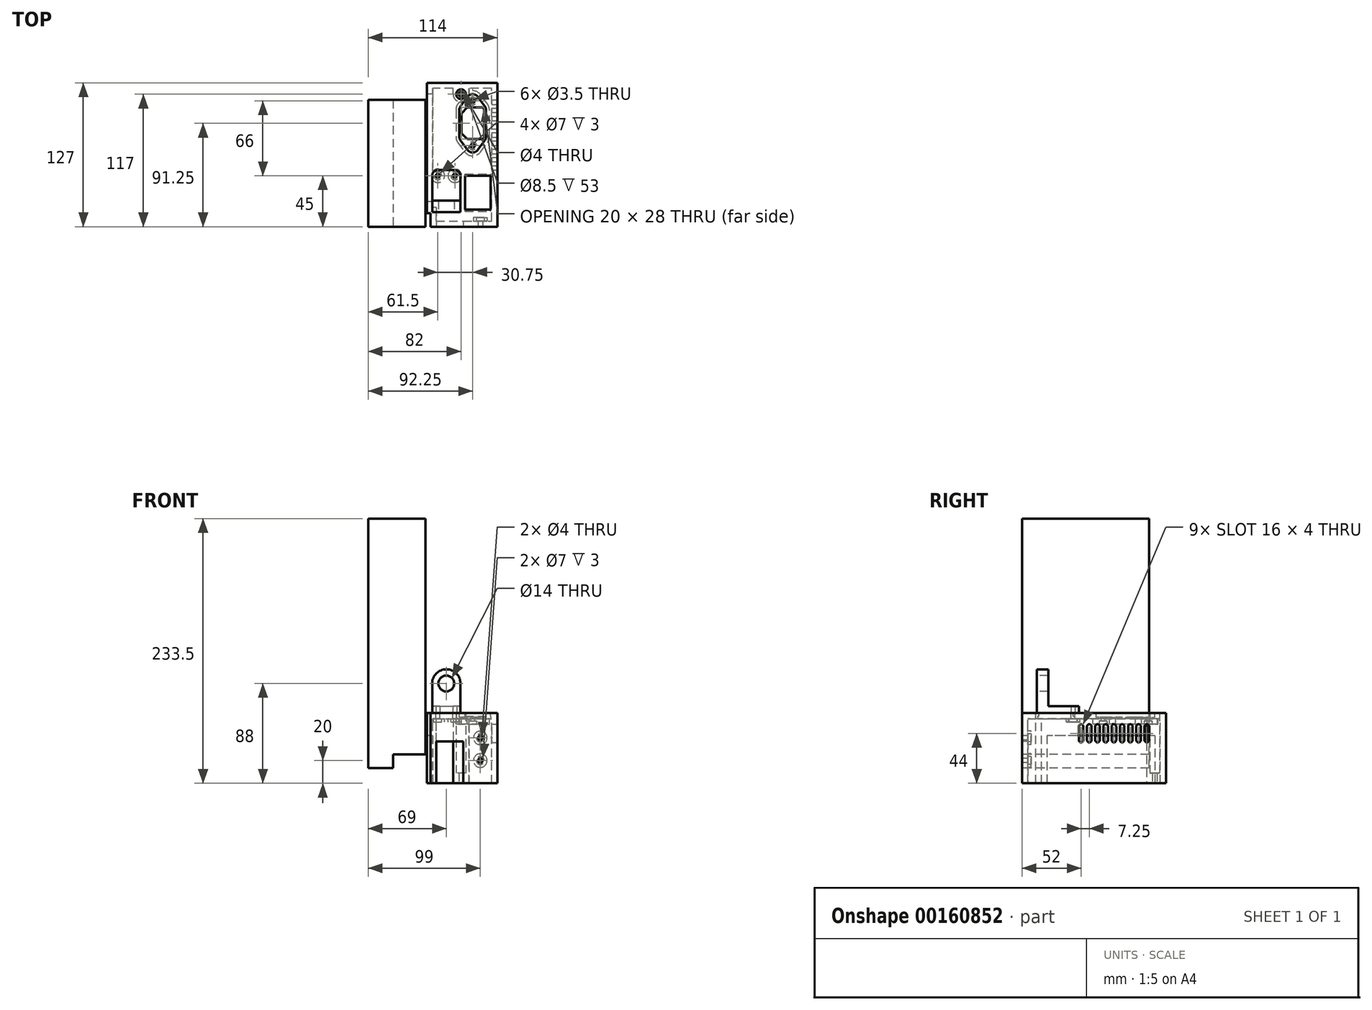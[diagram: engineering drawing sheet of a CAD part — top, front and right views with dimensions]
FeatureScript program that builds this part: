
annotation { "Feature Type Name" : "Feature", "Feature Type Description" : "" }
export const myFeature = defineFeature(function(context is Context, id is Id, definition is map)
    precondition{}
    {
        {
            var Q0;
            Q0=qCreatedBy(makeId("Front.planeOp"),FACE);
            var sketch = newSketch(context, id + "F0", { "sketchPlane" : qUnion([Q0])});
            skLineSegment(sketch, "E0", {"start": v(0, 13.5) * mm, "end": v(0, 233.5) * mm});
            skLineSegment(sketch, "E1", {"start": v(0, 233.5) * mm, "end": v(50.5, 233.5) * mm});
            skLineSegment(sketch, "E2", {"start": v(50.5, 233.5) * mm, "end": v(50.5, 25.5) * mm});
            skLineSegment(sketch, "E3", {"start": v(50.5, 25.5) * mm, "end": v(22, 25.5) * mm});
            skLineSegment(sketch, "E4", {"start": v(22, 25.5) * mm, "end": v(22, 13.5) * mm});
            skLineSegment(sketch, "E5", {"start": v(22, 13.5) * mm, "end": v(0, 13.5) * mm});
            skSolve(sketch);
        }
        {
            var Q0;
            Q0=qCreatedBy(makeId("Top.planeOp"),FACE);
            cPlane(context, id + "F1", {"entities" : qUnion([Q0]), "cplaneType" : CPlaneType.OFFSET, "offset" : 62 * mm, "width" : 150 * mm, "height" : 150 * mm});
        }
        {
            assignVariable(context, id + "F2", {"name" : "X", "anyValue" : 5});
        }
        {
            var Q0;
            Q0=qCreatedBy(id+"F1.planeOp",FACE);
            var sketch = newSketch(context, id + "F3", { "sketchPlane" : qUnion([Q0])});
            skLineSegment(sketch, "E6", {"start": v(55, 0) * mm, "end": v(114, 0) * mm});
            skLineSegment(sketch, "E7", {"start": v(114, 0) * mm, "end": v(114, 127) * mm});
            skLineSegment(sketch, "E8", {"start": v(114, 127) * mm, "end": v(52, 127) * mm});
            skLineSegment(sketch, "E9", {"start": v(52, 127) * mm, "end": v(52, 12) * mm});
            skLineSegment(sketch, "E10.bottom", {"start": v(85.5, 15) * mm, "end": v(108, 15) * mm});
            skLineSegment(sketch, "E10.top", {"start": v(85.5, 45) * mm, "end": v(108, 45) * mm});
            skLineSegment(sketch, "E10.left", {"start": v(85.5, 15) * mm, "end": v(85.5, 45) * mm});
            skLineSegment(sketch, "E10.right", {"start": v(108, 15) * mm, "end": v(108, 45) * mm});
            skLineSegment(sketch, "E11", {"start": v(52, 12) * mm, "end": v(55, 12) * mm});
            skLineSegment(sketch, "E12", {"start": v(55, 12) * mm, "end": v(55, 0) * mm});
            skPoint(sketch, "E13.orphan", {"position": v(52, 0) * mm});
            skCircle(sketch, "E14", {"center": v(61.5, 45) * mm, "radius": 1.75 * mm});
            skCircle(sketch, "E15", {"center": v(76.5, 45) * mm, "radius": 1.75 * mm});
            skLineSegment(sketch, "E16", {"start": v(61.5, 45) * mm, "end": v(76.5, 45) * mm, "construction": true});
            skPoint(sketch, "E17", {"position": v(69, 45) * mm});
            skPoint(sketch, "E18", {"position": v(83, 127) * mm});
            skSolve(sketch);
        }
        {
            var Q0;
            Q0 = qSketchRegion(id + "F3", true);
            extrude(context, id + "F4", {"entities" : qUnion([Q0]), "oppositeDirection" : true, "depth" : (getVariable(context, 'X')) * mm});
        }
        {
            var Q0;
            Q0=makeQuery(id+"F4.opExtrude","CAP_FACE",FACE,{"disambiguationData":[OSD([sQuery(id+"F3.wireOp",EDGE,"E6"),sQuery(id+"F3.wireOp",EDGE,"E7"),sQuery(id+"F3.wireOp",EDGE,"E8"),sQuery(id+"F3.wireOp",EDGE,"E9"),sQuery(id+"F3.wireOp",EDGE,"E10.bottom"),sQuery(id+"F3.wireOp",EDGE,"E10.top"),sQuery(id+"F3.wireOp",EDGE,"E10.left"),sQuery(id+"F3.wireOp",EDGE,"E10.right"),sQuery(id+"F3.wireOp",EDGE,"E11"),sQuery(id+"F3.wireOp",EDGE,"E12"),sQuery(id+"F3.wireOp",EDGE,"E14"),sQuery(id+"F3.wireOp",EDGE,"E15")])],"isStart":false});
            var sketch = newSketch(context, id + "F5", { "sketchPlane" : qUnion([Q0]), "disableImprinting" : false});
            skLineSegment(sketch, "E19", {"start": v(85.5, -30) * mm, "end": v(108, -30) * mm, "construction": true});
            skLineSegment(sketch, "E20.bottom", {"start": v(85.5, -45) * mm, "end": v(108, -45) * mm});
            skLineSegment(sketch, "E20.top", {"start": v(85.5, -46.5) * mm, "end": v(108, -46.5) * mm});
            skLineSegment(sketch, "E20.left", {"start": v(85.5, -45) * mm, "end": v(85.5, -46.5) * mm});
            skLineSegment(sketch, "E20.right", {"start": v(108, -45) * mm, "end": v(108, -46.5) * mm});
            skLineSegment(sketch, "E21.MirrorCS", {"start": v(108, -15) * mm, "end": v(108, -13.5) * mm});
            skLineSegment(sketch, "E22.MirrorCS", {"start": v(85.5, -15) * mm, "end": v(85.5, -13.5) * mm});
            skLineSegment(sketch, "E23.MirrorCS", {"start": v(85.5, -15) * mm, "end": v(108, -15) * mm});
            skLineSegment(sketch, "E24.MirrorCS", {"start": v(85.5, -13.5) * mm, "end": v(108, -13.5) * mm});
            skSolve(sketch);
        }
        {
            var Q0;
            Q0 = qSketchRegion(id + "F5", true);
            extrude(context, id + "F6", {"entities" : qUnion([Q0]), "operationType" : NewBodyOperationType.REMOVE, "oppositeDirection" : true, "depth" : 2 * mm});
        }
        {
            var Q0;
            Q0=makeQuery(id+"F4.opExtrude","SWEPT_FACE",FACE,{"disambiguationData":[OSD([sQuery(id+"F3.wireOp",EDGE,"E6")])]});
            var sketch = newSketch(context, id + "F7", { "sketchPlane" : qUnion([Q0])});
            skLineSegment(sketch, "E25.bottom", {"start": v(55, 57) * mm, "end": v(114, 57) * mm});
            skLineSegment(sketch, "E25.left", {"start": v(55, 57) * mm, "end": v(55, 37) * mm});
            skLineSegment(sketch, "E25.right", {"start": v(114, 57) * mm, "end": v(114, 0) * mm});
            skLineSegment(sketch, "E26", {"start": v(55, 37) * mm, "end": v(84, 37) * mm});
            skLineSegment(sketch, "E27", {"start": v(84, 37) * mm, "end": v(84, 0) * mm});
            skLineSegment(sketch, "E28", {"start": v(84, 0) * mm, "end": v(114, 0) * mm});
            skCircle(sketch, "E29", {"center": v(99, 20) * mm, "radius": 2 * mm});
            skCircle(sketch, "E30", {"center": v(99, 40) * mm, "radius": 2 * mm});
            skPoint(sketch, "E31", {"position": v(99, 0) * mm});
            skSolve(sketch);
        }
        {
            var Q0;
            Q0 = qSketchRegion(id + "F7", true);
            extrude(context, id + "F8", {"entities" : qUnion([Q0]), "operationType" : NewBodyOperationType.ADD, "oppositeDirection" : true, "depth" : (getVariable(context, 'X')) * mm});
        }
        {
            var Q0;
            Q0=makeQuery(id+"F4.opExtrude","CAP_FACE",FACE,{"disambiguationData":[OSD([sQuery(id+"F3.wireOp",EDGE,"E6"),sQuery(id+"F3.wireOp",EDGE,"E7"),sQuery(id+"F3.wireOp",EDGE,"E8"),sQuery(id+"F3.wireOp",EDGE,"E9"),sQuery(id+"F3.wireOp",EDGE,"E10.bottom"),sQuery(id+"F3.wireOp",EDGE,"E10.top"),sQuery(id+"F3.wireOp",EDGE,"E10.left"),sQuery(id+"F3.wireOp",EDGE,"E10.right"),sQuery(id+"F3.wireOp",EDGE,"E11"),sQuery(id+"F3.wireOp",EDGE,"E12")])],"isStart":false});
            var sketch = newSketch(context, id + "F9", { "sketchPlane" : qUnion([Q0])});
            skLineSegment(sketch, "E32", {"start": v(114, -5) * mm, "end": v(114, -127) * mm});
            skLineSegment(sketch, "E33", {"start": v(114, -127) * mm, "end": v(52, -127) * mm});
            skLineSegment(sketch, "E34", {"start": v(52, -127) * mm, "end": v(52, -12) * mm});
            skLineSegment(sketch, "E35", {"start": v(52, -12) * mm, "end": v(55, -12) * mm});
            skLineSegment(sketch, "E36", {"start": v(55, -12) * mm, "end": v(55, 0) * mm});
            skLineSegment(sketch, "E37", {"start": v(55, 0) * mm, "end": v(60, 0) * mm});
            skLineSegment(sketch, "E38", {"start": v(60, 0) * mm, "end": v(60, -17) * mm});
            skLineSegment(sketch, "E39", {"start": v(60, -17) * mm, "end": v(57, -17) * mm});
            skLineSegment(sketch, "E40", {"start": v(57, -122) * mm, "end": v(109, -122) * mm});
            skLineSegment(sketch, "E41", {"start": v(109, -122) * mm, "end": v(109, -5) * mm});
            skLineSegment(sketch, "E42", {"start": v(109, -5) * mm, "end": v(114, -5) * mm});
            skLineSegment(sketch, "E43", {"start": v(57, -17) * mm, "end": v(57, -122) * mm});
            skSolve(sketch);
        }
        {
            var Q0;
            Q0 = qSketchRegion(id + "F9", true);
            var Q1;
            Q1=qCreatedBy(makeId("Top.planeOp"),FACE);
            extrude(context, id + "F10", {"entities" : qUnion([Q0]), "operationType" : NewBodyOperationType.ADD, "endBound" : BoundingType.UP_TO_SURFACE, "endBoundEntityFace" : qUnion([Q1]), "depth" : 25 * mm});
        }
        {
            var Q0;
            Q0=qCreatedBy(makeId("Top.planeOp"),FACE);
            var sketch = newSketch(context, id + "F11", { "sketchPlane" : qUnion([Q0])});
            skCircle(sketch, "E44", {"center": v(82, 117) * mm, "radius": 7 * mm});
            skPoint(sketch, "E45", {"position": v(52, 127) * mm});
            skCircle(sketch, "E46", {"center": v(82, 117) * mm, "radius": 2 * mm});
            skLineSegment(sketch, "E47", {"start": v(75, 117) * mm, "end": v(75, 127) * mm});
            skLineSegment(sketch, "E48", {"start": v(75, 127) * mm, "end": v(89, 127) * mm});
            skLineSegment(sketch, "E49", {"start": v(89, 127) * mm, "end": v(89, 117) * mm});
            skSolve(sketch);
        }
        {
            var Q0;
            Q0 = qSketchRegion(id + "F11", true);
            var Q1;
            Q1=makeQuery(id+"F4.opExtrude","CAP_FACE",FACE,{"disambiguationData":[OSD([sQuery(id+"F3.wireOp",EDGE,"E6"),sQuery(id+"F3.wireOp",EDGE,"E7"),sQuery(id+"F3.wireOp",EDGE,"E8"),sQuery(id+"F3.wireOp",EDGE,"E9"),sQuery(id+"F3.wireOp",EDGE,"E10.bottom"),sQuery(id+"F3.wireOp",EDGE,"E10.top"),sQuery(id+"F3.wireOp",EDGE,"E10.left"),sQuery(id+"F3.wireOp",EDGE,"E10.right"),sQuery(id+"F3.wireOp",EDGE,"E11"),sQuery(id+"F3.wireOp",EDGE,"E12"),sQuery(id+"F3.wireOp",EDGE,"E14"),sQuery(id+"F3.wireOp",EDGE,"E15")])],"isStart":true});
            extrude(context, id + "F12", {"entities" : qUnion([Q0]), "operationType" : NewBodyOperationType.ADD, "endBound" : BoundingType.UP_TO_SURFACE, "endBoundEntityFace" : qUnion([Q1]), "depth" : 25 * mm});
        }
        {
            var Q0;
            Q0=makeQuery(id+"F4.opExtrude","CAP_FACE",FACE,{"disambiguationData":[OSD([sQuery(id+"F3.wireOp",EDGE,"E6"),sQuery(id+"F3.wireOp",EDGE,"E7"),sQuery(id+"F3.wireOp",EDGE,"E8"),sQuery(id+"F3.wireOp",EDGE,"E9"),sQuery(id+"F3.wireOp",EDGE,"E10.bottom"),sQuery(id+"F3.wireOp",EDGE,"E10.top"),sQuery(id+"F3.wireOp",EDGE,"E10.left"),sQuery(id+"F3.wireOp",EDGE,"E10.right"),sQuery(id+"F3.wireOp",EDGE,"icFeodHG-X67S-GUbe-anhc-zYEM1fz8yry0"),sQuery(id+"F3.wireOp",EDGE,"6k1QtSXw-TwQi-QSg0-uvi8-0hQTAuIMNpvk"),sQuery(id+"F3.wireOp",EDGE,"tgVIdKk2-un53-9VJQ-DeHb-1WSuqyKC1VRE"),sQuery(id+"F3.wireOp",EDGE,"f23b5b03-630f-4854-9769-42faad0535ed0.MirrorCS"),sQuery(id+"F3.wireOp",EDGE,"a012bc5f-21a9-49e4-83e2-b8ed56f6d75a0.MirrorCS"),sQuery(id+"F3.wireOp",EDGE,"6c684b62-b8df-48bf-a682-26947638c5150.MirrorCS"),sQuery(id+"F3.wireOp",EDGE,"226860c7-e29d-4859-8903-939a02a947c00.MirrorCS"),sQuery(id+"F3.wireOp",EDGE,"a3930372-3e52-4283-94ea-4f7785915df50.MirrorCS"),sQuery(id+"F3.wireOp",EDGE,"2bd0807f-86d2-4633-a58d-4318a14e78250.MirrorCS"),sQuery(id+"F3.wireOp",EDGE,"e933c2e2-a1c3-460c-bcf3-0e9317d1bf4b0.MirrorCS"),sQuery(id+"F3.wireOp",EDGE,"0f086fad-6bdd-4517-966f-ae18f11ac6380.MirrorCS"),sQuery(id+"F3.wireOp",EDGE,"3b35046c-a394-40a0-8ea3-9ca372d3b10c0.MirrorCS"),sQuery(id+"F3.wireOp",EDGE,"92acfec4-3e32-4bdd-830b-4b1668f26de1.filletArc"),sQuery(id+"F3.wireOp",EDGE,"2ca518d5-96dd-47ef-80e1-5cfa871b5b48.filletArc"),sQuery(id+"F3.wireOp",EDGE,"7e7fc31b-50f3-40aa-b3ab-8119e1af2ef3.filletArc"),sQuery(id+"F3.wireOp",EDGE,"9d7bcf72-4d73-4a1d-98b1-cddff58b6144.filletArc")])],"isStart":true});
            var sketch = newSketch(context, id + "F13", { "sketchPlane" : qUnion([Q0])});
            skLineSegment(sketch, "E50", {"start": v(92.25, 117) * mm, "end": v(92.25, 91.25) * mm, "construction": true});
            skLineSegment(sketch, "E51", {"start": v(92.25, 91.25) * mm, "end": v(104, 91.25) * mm, "construction": true});
            skLineSegment(sketch, "E52", {"start": v(104, 91.25) * mm, "end": v(104, 103.01) * mm});
            skLineSegment(sketch, "E53", {"start": v(102.81, 106.6) * mm, "end": v(96.75, 114.74) * mm});
            skArc(sketch, "E54", {"start": v(96.75, 114.74) * mm, "mid": v(94.77, 116.4) * mm, "end": v(92.25, 117) * mm});
            skArc(sketch, "E55.MirrorCS", {"start": v(87.75, 114.74) * mm, "mid": v(89.73, 116.4) * mm, "end": v(92.25, 117) * mm});
            skLineSegment(sketch, "E56.MirrorCS", {"start": v(81.69, 106.6) * mm, "end": v(87.75, 114.74) * mm});
            skLineSegment(sketch, "E57.MirrorCS", {"start": v(80.5, 91.25) * mm, "end": v(80.5, 103.01) * mm});
            skLineSegment(sketch, "E58.MirrorCS", {"start": v(80.5, 91.25) * mm, "end": v(80.5, 79.49) * mm});
            skLineSegment(sketch, "E59.MirrorCS", {"start": v(81.69, 75.9) * mm, "end": v(87.75, 67.76) * mm});
            skArc(sketch, "E60.MirrorCS", {"start": v(87.75, 67.76) * mm, "mid": v(89.73, 66.1) * mm, "end": v(92.25, 65.5) * mm});
            skArc(sketch, "E61.MirrorCS", {"start": v(96.75, 67.76) * mm, "mid": v(94.77, 66.1) * mm, "end": v(92.25, 65.5) * mm});
            skLineSegment(sketch, "E62.MirrorCS", {"start": v(102.81, 75.9) * mm, "end": v(96.75, 67.76) * mm});
            skLineSegment(sketch, "E63.MirrorCS", {"start": v(104, 91.25) * mm, "end": v(104, 79.49) * mm});
            skCircle(sketch, "E64", {"center": v(92.25, 111) * mm, "radius": 1.75 * mm, "construction": true});
            skCircle(sketch, "E65.MirrorC", {"center": v(92.25, 71.5) * mm, "radius": 1.75 * mm, "construction": true});
            skPoint(sketch, "E66.visualSharp", {"position": v(104, 105) * mm});
            skArc(sketch, "E66.filletArc", {"start": v(104, 103.01) * mm, "mid": v(103.7, 104.9) * mm, "end": v(102.81, 106.6) * mm});
            skPoint(sketch, "E67.visualSharp", {"position": v(80.5, 105) * mm});
            skArc(sketch, "E67.filletArc", {"start": v(81.69, 106.6) * mm, "mid": v(80.8, 104.9) * mm, "end": v(80.5, 103.01) * mm});
            skPoint(sketch, "E68.visualSharp", {"position": v(80.5, 77.5) * mm});
            skArc(sketch, "E68.filletArc", {"start": v(80.5, 79.49) * mm, "mid": v(80.8, 77.6) * mm, "end": v(81.69, 75.9) * mm});
            skPoint(sketch, "E69.visualSharp", {"position": v(104, 77.5) * mm});
            skArc(sketch, "E69.filletArc", {"start": v(102.81, 75.9) * mm, "mid": v(103.7, 77.6) * mm, "end": v(104, 79.49) * mm});
            skSolve(sketch);
        }
        {
            var Q0;
            Q0 = qSketchRegion(id + "F13", true);
            extrude(context, id + "F14", {"entities" : qUnion([Q0]), "operationType" : NewBodyOperationType.REMOVE, "oppositeDirection" : true, "depth" : 3.8 * mm});
        }
        {
            var Q0;
            Q0=makeQuery(id+"F14.boolean.opBoolean","COPY",FACE,{"derivedFrom":makeQuery(id+"F14.opExtrude","CAP_FACE",FACE,{"disambiguationData":[OSD([sQuery(id+"F13.wireOp",EDGE,"E52"),sQuery(id+"F13.wireOp",EDGE,"E53"),sQuery(id+"F13.wireOp",EDGE,"E54"),sQuery(id+"F13.wireOp",EDGE,"E55.MirrorCS"),sQuery(id+"F13.wireOp",EDGE,"E56.MirrorCS"),sQuery(id+"F13.wireOp",EDGE,"E57.MirrorCS"),sQuery(id+"F13.wireOp",EDGE,"E58.MirrorCS"),sQuery(id+"F13.wireOp",EDGE,"E59.MirrorCS"),sQuery(id+"F13.wireOp",EDGE,"E60.MirrorCS"),sQuery(id+"F13.wireOp",EDGE,"E61.MirrorCS"),sQuery(id+"F13.wireOp",EDGE,"E62.MirrorCS"),sQuery(id+"F13.wireOp",EDGE,"E63.MirrorCS"),sQuery(id+"F13.wireOp",EDGE,"E66.filletArc"),sQuery(id+"F13.wireOp",EDGE,"E67.filletArc"),sQuery(id+"F13.wireOp",EDGE,"E68.filletArc"),sQuery(id+"F13.wireOp",EDGE,"E69.filletArc")])],"isStart":false})});
            var sketch = newSketch(context, id + "F15", { "sketchPlane" : qUnion([Q0])});
            skPoint(sketch, "E70", {"position": v(92.25, 91.25) * mm});
            skLineSegment(sketch, "E71", {"start": v(102.25, 91.25) * mm, "end": v(102.25, 103.25) * mm});
            skLineSegment(sketch, "E72", {"start": v(100.25, 105.25) * mm, "end": v(87.5, 105.25) * mm});
            skLineSegment(sketch, "E73", {"start": v(87.5, 105.25) * mm, "end": v(82.25, 100) * mm});
            skLineSegment(sketch, "E74", {"start": v(82.25, 100) * mm, "end": v(82.25, 91.25) * mm});
            skLineSegment(sketch, "E75", {"start": v(82.25, 91.25) * mm, "end": v(102.25, 91.25) * mm, "construction": true});
            skLineSegment(sketch, "E76.MirrorCS", {"start": v(82.25, 82.5) * mm, "end": v(82.25, 91.25) * mm});
            skLineSegment(sketch, "E77.MirrorCS", {"start": v(87.5, 77.25) * mm, "end": v(82.25, 82.5) * mm});
            skLineSegment(sketch, "E78.MirrorCS", {"start": v(100.25, 77.25) * mm, "end": v(87.5, 77.25) * mm});
            skLineSegment(sketch, "E79.MirrorCS", {"start": v(102.25, 91.25) * mm, "end": v(102.25, 79.25) * mm});
            skCircle(sketch, "E80", {"center": v(92.25, 111) * mm, "radius": 1.75 * mm});
            skCircle(sketch, "E81.MirrorC", {"center": v(92.25, 71.5) * mm, "radius": 1.75 * mm});
            skPoint(sketch, "E82.visualSharp", {"position": v(102.25, 105.25) * mm});
            skArc(sketch, "E82.filletArc", {"start": v(102.25, 103.25) * mm, "mid": v(101.66, 104.66) * mm, "end": v(100.25, 105.25) * mm});
            skPoint(sketch, "E83.visualSharp", {"position": v(102.25, 77.25) * mm});
            skArc(sketch, "E83.filletArc", {"start": v(100.25, 77.25) * mm, "mid": v(101.66, 77.84) * mm, "end": v(102.25, 79.25) * mm});
            skSolve(sketch);
        }
        {
            var Q0;
            Q0 = qSketchRegion(id + "F15", true);
            extrude(context, id + "F16", {"entities" : qUnion([Q0]), "operationType" : NewBodyOperationType.REMOVE, "oppositeDirection" : true, "depth" : 25 * mm});
        }
        {
            var Q0;
            Q0=makeQuery(id+"F4.opExtrude","CAP_FACE",FACE,{"disambiguationData":[OSD([sQuery(id+"F3.wireOp",EDGE,"E6"),sQuery(id+"F3.wireOp",EDGE,"E7"),sQuery(id+"F3.wireOp",EDGE,"E8"),sQuery(id+"F3.wireOp",EDGE,"E9"),sQuery(id+"F3.wireOp",EDGE,"E10.bottom"),sQuery(id+"F3.wireOp",EDGE,"E10.top"),sQuery(id+"F3.wireOp",EDGE,"E10.left"),sQuery(id+"F3.wireOp",EDGE,"E10.right")])],"isStart":false});
            var sketch = newSketch(context, id + "F17", { "sketchPlane" : qUnion([Q0])});
            skArc(sketch, "E84.0", {"start": v(105.22, -74.11) * mm, "mid": v(106.54, -76.66) * mm, "end": v(107, -79.49) * mm});
            skLineSegment(sketch, "E84.1", {"start": v(99.16, -65.97) * mm, "end": v(105.22, -74.11) * mm});
            skArc(sketch, "E84.2", {"start": v(92.25, -62.5) * mm, "mid": v(96.11, -63.42) * mm, "end": v(99.16, -65.97) * mm});
            skArc(sketch, "E84.3", {"start": v(85.34, -65.97) * mm, "mid": v(88.39, -63.42) * mm, "end": v(92.25, -62.5) * mm});
            skLineSegment(sketch, "E84.4", {"start": v(79.28, -74.11) * mm, "end": v(85.34, -65.97) * mm});
            skArc(sketch, "E84.5", {"start": v(99.16, -116.53) * mm, "mid": v(96.11, -119.08) * mm, "end": v(92.25, -120) * mm});
            skLineSegment(sketch, "E84.6", {"start": v(105.22, -108.39) * mm, "end": v(99.16, -116.53) * mm});
            skArc(sketch, "E84.7", {"start": v(107, -103.01) * mm, "mid": v(106.54, -105.84) * mm, "end": v(105.22, -108.39) * mm});
            skLineSegment(sketch, "E84.8", {"start": v(107, -89.5) * mm, "end": v(107, -103.01) * mm});
            skArc(sketch, "E84.9", {"start": v(92.25, -120) * mm, "mid": v(88.39, -119.08) * mm, "end": v(85.34, -116.53) * mm});
            skLineSegment(sketch, "E84.10", {"start": v(85.34, -116.53) * mm, "end": v(79.28, -108.39) * mm});
            skArc(sketch, "E84.11", {"start": v(79.28, -108.39) * mm, "mid": v(77.96, -105.84) * mm, "end": v(77.5, -103.01) * mm});
            skLineSegment(sketch, "E84.12", {"start": v(77.5, -103.01) * mm, "end": v(77.5, -89.5) * mm});
            skLineSegment(sketch, "E84.13", {"start": v(77.5, -89.5) * mm, "end": v(77.5, -79.49) * mm});
            skLineSegment(sketch, "E84.14", {"start": v(107, -79.49) * mm, "end": v(107, -89.5) * mm});
            skArc(sketch, "E84.15", {"start": v(77.5, -79.49) * mm, "mid": v(77.96, -76.66) * mm, "end": v(79.28, -74.11) * mm});
            skLineSegment(sketch, "E85", {"start": v(100.25, -105.25) * mm, "end": v(87.5, -105.25) * mm});
            skLineSegment(sketch, "E86", {"start": v(87.5, -105.25) * mm, "end": v(82.25, -100) * mm});
            skLineSegment(sketch, "E87", {"start": v(82.25, -100) * mm, "end": v(82.25, -82.5) * mm});
            skLineSegment(sketch, "E88", {"start": v(82.25, -82.5) * mm, "end": v(87.5, -77.25) * mm});
            skLineSegment(sketch, "E89", {"start": v(87.5, -77.25) * mm, "end": v(100.25, -77.25) * mm});
            skArc(sketch, "E90", {"start": v(102.25, -79.25) * mm, "mid": v(101.66, -77.84) * mm, "end": v(100.25, -77.25) * mm});
            skArc(sketch, "E91", {"start": v(100.25, -105.25) * mm, "mid": v(101.66, -104.66) * mm, "end": v(102.25, -103.25) * mm});
            skLineSegment(sketch, "E92", {"start": v(102.25, -103.25) * mm, "end": v(102.25, -79.25) * mm});
            skCircle(sketch, "E93", {"center": v(92.25, -111) * mm, "radius": 1.75 * mm});
            skCircle(sketch, "E94", {"center": v(92.25, -71.5) * mm, "radius": 1.75 * mm});
            skSolve(sketch);
        }
        {
            var Q0;
            Q0 = qSketchRegion(id + "F17", true);
            extrude(context, id + "F18", {"entities" : qUnion([Q0]), "operationType" : NewBodyOperationType.ADD, "depth" : 5 * mm});
        }
        {
            var Q0;
            Q0=qCreatedBy(makeId("Top.planeOp"),FACE);
            var sketch = newSketch(context, id + "F19", { "sketchPlane" : qUnion([Q0])});
            skCircle(sketch, "E95", {"center": v(82, 117) * mm, "radius": 4.25 * mm});
            skSolve(sketch);
        }
        {
            var Q0;
            Q0 = qSketchRegion(id + "F19", true);
            extrude(context, id + "F20", {"entities" : qUnion([Q0]), "operationType" : NewBodyOperationType.REMOVE, "endBound" : BoundingType.THROUGH_ALL, "depth" : 25 * mm, "hasSecondDirection" : true, "secondDirectionOppositeDirection" : false, "secondDirectionDepth" : 9 * mm});
        }
        {
            var Q0;
            Q0 = qSketchRegion(id + "F0", true);
            extrude(context, id + "F21", {"entities" : qUnion([Q0]), "oppositeDirection" : true, "depth" : 112 * mm});
        }
        {
            var Q0;
            Q0=makeQuery(id+"F10.boolean.opBoolean","MERGE",FACE,{"derivedFrom":[makeQuery(id+"F4.opExtrude","SWEPT_FACE",FACE,{"disambiguationData":[OSD([sQuery(id+"F3.wireOp",EDGE,"E9")])]}),makeQuery(id+"F10.opExtrude","SWEPT_FACE",FACE,{"disambiguationData":[OSD([sQuery(id+"F9.wireOp",EDGE,"E34")])]})]});
            var sketch = newSketch(context, id + "F22", { "sketchPlane" : qUnion([Q0])});
            skLineSegment(sketch, "E96.bottom", {"start": v(-117, 42) * mm, "end": v(-22, 42) * mm});
            skLineSegment(sketch, "E96.top", {"start": v(-117, 0) * mm, "end": v(-22, 0) * mm});
            skLineSegment(sketch, "E96.left", {"start": v(-117, 42) * mm, "end": v(-117, 0) * mm});
            skLineSegment(sketch, "E96.right", {"start": v(-22, 42) * mm, "end": v(-22, 0) * mm});
            skSolve(sketch);
        }
        {
            var Q0;
            Q0 = qSketchRegion(id + "F22", true);
            var Q1;
            Q1=makeQuery(id+"F10.opExtrude","SWEPT_FACE",FACE,{"disambiguationData":[OSD([sQuery(id+"F9.wireOp",EDGE,"E43")])]});
            extrude(context, id + "F23", {"entities" : qUnion([Q0]), "operationType" : NewBodyOperationType.REMOVE, "flatOperationType" : FlatOperationType.REMOVE, "endBound" : BoundingType.UP_TO_SURFACE, "oppositeDirection" : true, "endBoundEntityFace" : qUnion([Q1]), "offsetDistance" : 25 * mm, "depth" : 25 * mm, "domain" : OperationDomain.MODEL});
        }
        {
            var Q0;
            Q0=makeQuery(id+"F18.opExtrude","CAP_FACE",FACE,{"disambiguationData":[OSD([sQuery(id+"F17.wireOp",EDGE,"E84.0"),sQuery(id+"F17.wireOp",EDGE,"E84.1"),sQuery(id+"F17.wireOp",EDGE,"E84.2"),sQuery(id+"F17.wireOp",EDGE,"E84.3"),sQuery(id+"F17.wireOp",EDGE,"E84.4"),sQuery(id+"F17.wireOp",EDGE,"E84.5"),sQuery(id+"F17.wireOp",EDGE,"E84.6"),sQuery(id+"F17.wireOp",EDGE,"E84.7"),sQuery(id+"F17.wireOp",EDGE,"E84.8"),sQuery(id+"F17.wireOp",EDGE,"E84.9"),sQuery(id+"F17.wireOp",EDGE,"E84.10"),sQuery(id+"F17.wireOp",EDGE,"E84.11"),sQuery(id+"F17.wireOp",EDGE,"E84.12"),sQuery(id+"F17.wireOp",EDGE,"E84.13"),sQuery(id+"F17.wireOp",EDGE,"E84.14"),sQuery(id+"F17.wireOp",EDGE,"E84.15"),sQuery(id+"F17.wireOp",EDGE,"E85"),sQuery(id+"F17.wireOp",EDGE,"E86"),sQuery(id+"F17.wireOp",EDGE,"E87"),sQuery(id+"F17.wireOp",EDGE,"E88"),sQuery(id+"F17.wireOp",EDGE,"E89"),sQuery(id+"F17.wireOp",EDGE,"E90"),sQuery(id+"F17.wireOp",EDGE,"E91"),sQuery(id+"F17.wireOp",EDGE,"E92"),sQuery(id+"F17.wireOp",EDGE,"E93"),sQuery(id+"F17.wireOp",EDGE,"E94")])],"isStart":false});
            var sketch = newSketch(context, id + "F24", { "sketchPlane" : qUnion([Q0])});
            skCircle(sketch, "E97", {"center": v(92.25, -71.5) * mm, "radius": 3.5 * mm});
            skCircle(sketch, "E98", {"center": v(92.25, -111) * mm, "radius": 3.5 * mm});
            skSolve(sketch);
        }
        {
            var Q0;
            Q0 = qSketchRegion(id + "F24", true);
            extrude(context, id + "F25", {"entities" : qUnion([Q0]), "operationType" : NewBodyOperationType.REMOVE, "oppositeDirection" : true, "depth" : 3 * mm});
        }
        {
            var Q0;
            Q0=makeQuery(id+"F4.opExtrude","CAP_FACE",FACE,{"disambiguationData":[OSD([sQuery(id+"F3.wireOp",EDGE,"E6"),sQuery(id+"F3.wireOp",EDGE,"E7"),sQuery(id+"F3.wireOp",EDGE,"E8"),sQuery(id+"F3.wireOp",EDGE,"E9"),sQuery(id+"F3.wireOp",EDGE,"E10.bottom"),sQuery(id+"F3.wireOp",EDGE,"E10.top"),sQuery(id+"F3.wireOp",EDGE,"E10.left"),sQuery(id+"F3.wireOp",EDGE,"E10.right"),sQuery(id+"F3.wireOp",EDGE,"E11"),sQuery(id+"F3.wireOp",EDGE,"E12"),sQuery(id+"F3.wireOp",EDGE,"E14"),sQuery(id+"F3.wireOp",EDGE,"E15")])],"isStart":false});
            var sketch = newSketch(context, id + "F26", { "sketchPlane" : qUnion([Q0])});
            skCircle(sketch, "E99", {"center": v(76.5, -45) * mm, "radius": 3.5 * mm});
            skCircle(sketch, "E100", {"center": v(76.5, -45) * mm, "radius": 6 * mm});
            skLineSegment(sketch, "E101", {"start": v(76.5, -45) * mm, "end": v(61.5, -45) * mm, "construction": true});
            skLineSegment(sketch, "E102", {"start": v(69, -45) * mm, "end": v(69, -39.5) * mm, "construction": true});
            skCircle(sketch, "E103.MirrorC", {"center": v(61.5, -45) * mm, "radius": 6 * mm});
            skCircle(sketch, "E104.MirrorC", {"center": v(61.5, -45) * mm, "radius": 3.5 * mm});
            skSolve(sketch);
        }
        {
            var Q0;
            Q0 = qSketchRegion(id + "F26", true);
            extrude(context, id + "F27", {"entities" : qUnion([Q0]), "operationType" : NewBodyOperationType.ADD, "depth" : 3 * mm});
        }
        {
            var Q0;
            Q0=makeQuery(id+"F10.boolean.opBoolean","MERGE",FACE,{"derivedFrom":[makeQuery(id+"F8.boolean.opBoolean","MERGE",FACE,{"derivedFrom":[makeQuery(id+"F4.opExtrude","SWEPT_FACE",FACE,{"disambiguationData":[OSD([sQuery(id+"F3.wireOp",EDGE,"E7")])]}),makeQuery(id+"F8.opExtrude","SWEPT_FACE",FACE,{"disambiguationData":[OSD([sQuery(id+"F7.wireOp",EDGE,"E25.right")])]})]}),makeQuery(id+"F10.opExtrude","SWEPT_FACE",FACE,{"disambiguationData":[OSD([sQuery(id+"F9.wireOp",EDGE,"E32")])]})]});
            var sketch = newSketch(context, id + "F28", { "sketchPlane" : qUnion([Q0])});
            skLineSegment(sketch, "E105", {"start": v(50, 50) * mm, "end": v(50, 38) * mm});
            skLineSegment(sketch, "E106", {"start": v(54, 50) * mm, "end": v(54, 38) * mm});
            skArc(sketch, "E107", {"start": v(54, 50) * mm, "mid": v(52, 52) * mm, "end": v(50, 50) * mm});
            skArc(sketch, "E108", {"start": v(50, 38) * mm, "mid": v(52, 36) * mm, "end": v(54, 38) * mm});
            skPoint(sketch, "E109", {"position": v(52, 52) * mm});
            skArc(sketch, "E110.1.0.0", {"start": v(57.25, 38) * mm, "mid": v(59.25, 36) * mm, "end": v(61.25, 38) * mm});
            skLineSegment(sketch, "E110.1.0.1", {"start": v(61.25, 50) * mm, "end": v(61.25, 38) * mm});
            skLineSegment(sketch, "E110.1.0.2", {"start": v(57.25, 50) * mm, "end": v(57.25, 38) * mm});
            skPoint(sketch, "E110.1.0.3", {"position": v(59.25, 52) * mm});
            skArc(sketch, "E110.1.0.4", {"start": v(61.25, 50) * mm, "mid": v(59.25, 52) * mm, "end": v(57.25, 50) * mm});
            skArc(sketch, "E110.2.0.0", {"start": v(64.5, 38) * mm, "mid": v(66.5, 36) * mm, "end": v(68.5, 38) * mm});
            skLineSegment(sketch, "E110.2.0.1", {"start": v(68.5, 50) * mm, "end": v(68.5, 38) * mm});
            skLineSegment(sketch, "E110.2.0.2", {"start": v(64.5, 50) * mm, "end": v(64.5, 38) * mm});
            skPoint(sketch, "E110.2.0.3", {"position": v(66.5, 52) * mm});
            skArc(sketch, "E110.2.0.4", {"start": v(68.5, 50) * mm, "mid": v(66.5, 52) * mm, "end": v(64.5, 50) * mm});
            skArc(sketch, "E110.3.0.0", {"start": v(71.75, 38) * mm, "mid": v(73.75, 36) * mm, "end": v(75.75, 38) * mm});
            skLineSegment(sketch, "E110.3.0.1", {"start": v(75.75, 50) * mm, "end": v(75.75, 38) * mm});
            skLineSegment(sketch, "E110.3.0.2", {"start": v(71.75, 50) * mm, "end": v(71.75, 38) * mm});
            skPoint(sketch, "E110.3.0.3", {"position": v(73.75, 52) * mm});
            skArc(sketch, "E110.3.0.4", {"start": v(75.75, 50) * mm, "mid": v(73.75, 52) * mm, "end": v(71.75, 50) * mm});
            skArc(sketch, "E110.4.0.0", {"start": v(79, 38) * mm, "mid": v(81, 36) * mm, "end": v(83, 38) * mm});
            skLineSegment(sketch, "E110.4.0.1", {"start": v(83, 50) * mm, "end": v(83, 38) * mm});
            skLineSegment(sketch, "E110.4.0.2", {"start": v(79, 50) * mm, "end": v(79, 38) * mm});
            skPoint(sketch, "E110.4.0.3", {"position": v(81, 52) * mm});
            skArc(sketch, "E110.4.0.4", {"start": v(83, 50) * mm, "mid": v(81, 52) * mm, "end": v(79, 50) * mm});
            skArc(sketch, "E110.5.0.0", {"start": v(86.25, 38) * mm, "mid": v(88.25, 36) * mm, "end": v(90.25, 38) * mm});
            skLineSegment(sketch, "E110.5.0.1", {"start": v(90.25, 50) * mm, "end": v(90.25, 38) * mm});
            skLineSegment(sketch, "E110.5.0.2", {"start": v(86.25, 50) * mm, "end": v(86.25, 38) * mm});
            skPoint(sketch, "E110.5.0.3", {"position": v(88.25, 52) * mm});
            skArc(sketch, "E110.5.0.4", {"start": v(90.25, 50) * mm, "mid": v(88.25, 52) * mm, "end": v(86.25, 50) * mm});
            skArc(sketch, "E110.6.0.0", {"start": v(93.5, 38) * mm, "mid": v(95.5, 36) * mm, "end": v(97.5, 38) * mm});
            skLineSegment(sketch, "E110.6.0.1", {"start": v(97.5, 50) * mm, "end": v(97.5, 38) * mm});
            skLineSegment(sketch, "E110.6.0.2", {"start": v(93.5, 50) * mm, "end": v(93.5, 38) * mm});
            skPoint(sketch, "E110.6.0.3", {"position": v(95.5, 52) * mm});
            skArc(sketch, "E110.6.0.4", {"start": v(97.5, 50) * mm, "mid": v(95.5, 52) * mm, "end": v(93.5, 50) * mm});
            skArc(sketch, "E110.7.0.0", {"start": v(100.75, 38) * mm, "mid": v(102.75, 36) * mm, "end": v(104.75, 38) * mm});
            skLineSegment(sketch, "E110.7.0.1", {"start": v(104.75, 50) * mm, "end": v(104.75, 38) * mm});
            skLineSegment(sketch, "E110.7.0.2", {"start": v(100.75, 50) * mm, "end": v(100.75, 38) * mm});
            skPoint(sketch, "E110.7.0.3", {"position": v(102.75, 52) * mm});
            skArc(sketch, "E110.7.0.4", {"start": v(104.75, 50) * mm, "mid": v(102.75, 52) * mm, "end": v(100.75, 50) * mm});
            skLineSegment(sketch, "E110.direction1", {"start": v(50, 38) * mm, "end": v(57.25, 38) * mm, "construction": true});
            skArc(sketch, "E111.0.8.0", {"start": v(108, 38) * mm, "mid": v(110, 36) * mm, "end": v(112, 38) * mm});
            skLineSegment(sketch, "E111.4.8.0", {"start": v(112, 50) * mm, "end": v(112, 38) * mm});
            skLineSegment(sketch, "E111.7.8.0", {"start": v(108, 50) * mm, "end": v(108, 38) * mm});
            skPoint(sketch, "E111.10.8.0", {"position": v(110, 52) * mm});
            skArc(sketch, "E111.11.8.0", {"start": v(112, 50) * mm, "mid": v(110, 52) * mm, "end": v(108, 50) * mm});
            skSolve(sketch);
        }
        {
            var Q0;
            Q0 = qSketchRegion(id + "F28", true);
            var Q1;
            Q1=makeQuery(id+"F10.opExtrude","SWEPT_FACE",FACE,{"disambiguationData":[OSD([sQuery(id+"F9.wireOp",EDGE,"E41")])]});
            extrude(context, id + "F29", {"entities" : qUnion([Q0]), "operationType" : NewBodyOperationType.REMOVE, "endBound" : BoundingType.UP_TO_SURFACE, "oppositeDirection" : true, "endBoundEntityFace" : qUnion([Q1]), "depth" : 25 * mm});
        }
        {
            var Q0;
            Q0=makeQuery(id+"F8.opExtrude","CAP_FACE",FACE,{"disambiguationData":[OSD([sQuery(id+"F7.wireOp",EDGE,"E25.bottom"),sQuery(id+"F7.wireOp",EDGE,"E25.left"),sQuery(id+"F7.wireOp",EDGE,"E25.right"),sQuery(id+"F7.wireOp",EDGE,"E26"),sQuery(id+"F7.wireOp",EDGE,"E27"),sQuery(id+"F7.wireOp",EDGE,"E28"),sQuery(id+"F7.wireOp",EDGE,"E29"),sQuery(id+"F7.wireOp",EDGE,"E30")])],"isStart":false});
            var sketch = newSketch(context, id + "F30", { "sketchPlane" : qUnion([Q0])});
            skCircle(sketch, "E112", {"center": v(-99, 20) * mm, "radius": 3.5 * mm});
            skCircle(sketch, "E113", {"center": v(-99, 40) * mm, "radius": 3.5 * mm});
            skCircle(sketch, "E114", {"center": v(-99, 20) * mm, "radius": 6 * mm});
            skCircle(sketch, "E115", {"center": v(-99, 40) * mm, "radius": 6 * mm});
            skSolve(sketch);
        }
        {
            var Q0;
            Q0 = qSketchRegion(id + "F30", true);
            extrude(context, id + "F31", {"entities" : qUnion([Q0]), "operationType" : NewBodyOperationType.ADD, "depth" : 3 * mm});
        }
        {
            var Q0;
            Q0=makeQuery(id+"F4.opExtrude","CAP_FACE",FACE,{"disambiguationData":[OSD([sQuery(id+"F3.wireOp",EDGE,"E6"),sQuery(id+"F3.wireOp",EDGE,"E7"),sQuery(id+"F3.wireOp",EDGE,"E8"),sQuery(id+"F3.wireOp",EDGE,"E9"),sQuery(id+"F3.wireOp",EDGE,"E10.bottom"),sQuery(id+"F3.wireOp",EDGE,"E10.top"),sQuery(id+"F3.wireOp",EDGE,"E10.left"),sQuery(id+"F3.wireOp",EDGE,"E10.right"),sQuery(id+"F3.wireOp",EDGE,"E11"),sQuery(id+"F3.wireOp",EDGE,"E12"),sQuery(id+"F3.wireOp",EDGE,"E14"),sQuery(id+"F3.wireOp",EDGE,"E15")])],"isStart":true});
            var sketch = newSketch(context, id + "F32", { "sketchPlane" : qUnion([Q0])});
            skLineSegment(sketch, "E116.bottom", {"start": v(61.5, 50) * mm, "end": v(76.5, 50) * mm});
            skLineSegment(sketch, "E116.top", {"start": v(56.5, 13) * mm, "end": v(81.5, 13) * mm});
            skLineSegment(sketch, "E116.left", {"start": v(56.5, 45) * mm, "end": v(56.5, 13) * mm});
            skLineSegment(sketch, "E116.right", {"start": v(81.5, 45) * mm, "end": v(81.5, 13) * mm});
            skPoint(sketch, "E117.visualSharp", {"position": v(56.5, 50) * mm});
            skArc(sketch, "E117.filletArc", {"start": v(61.5, 50) * mm, "mid": v(57.96, 48.54) * mm, "end": v(56.5, 45) * mm});
            skPoint(sketch, "E118.visualSharp", {"position": v(81.5, 50) * mm});
            skArc(sketch, "E118.filletArc", {"start": v(81.5, 45) * mm, "mid": v(80.04, 48.54) * mm, "end": v(76.5, 50) * mm});
            skPoint(sketch, "E119.visualSharp", {"position": v(81.5, 13) * mm});
            skPoint(sketch, "E120.visualSharp", {"position": v(56.5, 13) * mm});
            skPoint(sketch, "E121", {"position": v(69, 50) * mm});
            skLineSegment(sketch, "E122", {"start": v(61.5, 45) * mm, "end": v(76.5, 45) * mm, "construction": true});
            skPoint(sketch, "E123", {"position": v(69, 45) * mm});
            skCircle(sketch, "E124", {"center": v(76.5, 45) * mm, "radius": 1.75 * mm});
            skCircle(sketch, "E125", {"center": v(61.5, 45) * mm, "radius": 1.75 * mm});
            skSolve(sketch);
        }
        {
            var Q0;
            Q0 = qSketchRegion(id + "F32", true);
            extrude(context, id + "F33", {"entities" : qUnion([Q0]), "depth" : 6 * mm});
        }
        {
            var Q0;
            Q0=makeQuery(id+"F33.opExtrude","SWEPT_FACE",FACE,{"disambiguationData":[OSD([sQuery(id+"F32.wireOp",EDGE,"E116.top")])]});
            var sketch = newSketch(context, id + "F34", { "sketchPlane" : qUnion([Q0])});
            skLineSegment(sketch, "E126.bottom", {"start": v(56.5, 68) * mm, "end": v(81.5, 68) * mm});
            skLineSegment(sketch, "E126.left", {"start": v(56.5, 68) * mm, "end": v(56.5, 88) * mm});
            skLineSegment(sketch, "E126.right", {"start": v(81.5, 68) * mm, "end": v(81.5, 88) * mm});
            skArc(sketch, "E127", {"start": v(81.5, 88) * mm, "mid": v(69, 100.5) * mm, "end": v(56.5, 88) * mm});
            skCircle(sketch, "E128", {"center": v(69, 88) * mm, "radius": 7 * mm});
            skSolve(sketch);
        }
        {
            var Q0;
            Q0 = qSketchRegion(id + "F34", true);
            extrude(context, id + "F35", {"entities" : qUnion([Q0]), "operationType" : NewBodyOperationType.ADD, "oppositeDirection" : true, "depth" : 10 * mm});
        }
    });
